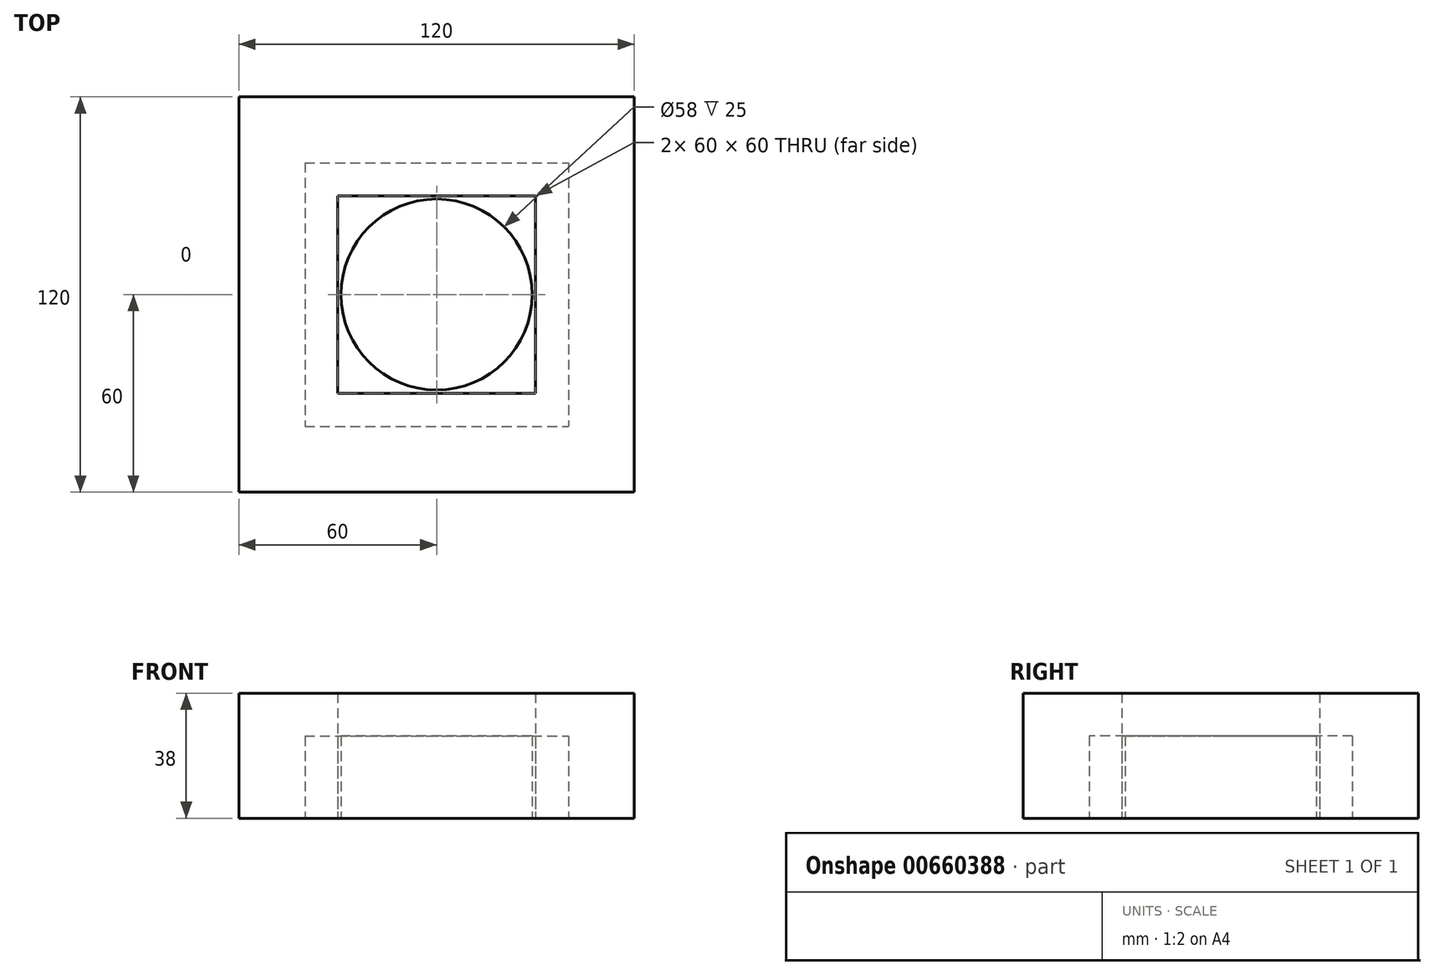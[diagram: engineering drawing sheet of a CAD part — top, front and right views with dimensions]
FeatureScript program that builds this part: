
annotation { "Feature Type Name" : "Feature", "Feature Type Description" : "" }
export const myFeature = defineFeature(function(context is Context, id is Id, definition is map)
    precondition{}
    {
        {
            var Q0;
            Q0=qCreatedBy(makeId("Top.planeOp"),FACE);
            var sketch = newSketch(context, id + "F0", { "sketchPlane" : qUnion([Q0])});
            skLineSegment(sketch, "E0.bottom", {"start": v(-60, 60) * mm, "end": v(60, 60) * mm});
            skLineSegment(sketch, "E0.top", {"start": v(-60, -60) * mm, "end": v(60, -60) * mm});
            skLineSegment(sketch, "E0.left", {"start": v(-60, 60) * mm, "end": v(-60, -60) * mm});
            skLineSegment(sketch, "E0.right", {"start": v(60, 60) * mm, "end": v(60, -60) * mm});
            skLineSegment(sketch, "E1.bottom", {"start": v(-40, 40) * mm, "end": v(40, 40) * mm});
            skLineSegment(sketch, "E1.top", {"start": v(-40, -40) * mm, "end": v(40, -40) * mm});
            skLineSegment(sketch, "E1.left", {"start": v(-40, 40) * mm, "end": v(-40, -40) * mm});
            skLineSegment(sketch, "E1.right", {"start": v(40, 40) * mm, "end": v(40, -40) * mm});
            skLineSegment(sketch, "E2.bottom", {"start": v(-30, -30) * mm, "end": v(30, -30) * mm});
            skLineSegment(sketch, "E2.top", {"start": v(-30, 30) * mm, "end": v(30, 30) * mm});
            skLineSegment(sketch, "E2.left", {"start": v(-30, -30) * mm, "end": v(-30, 30) * mm});
            skLineSegment(sketch, "E2.right", {"start": v(30, -30) * mm, "end": v(30, 30) * mm});
            skCircle(sketch, "E3", {"center": v(0, 0) * mm, "radius": 29 * mm});
            skSolve(sketch);
        }
        {
            var Q0;
            Q0=makeQuery(id+"F0.imprint","IMPRINT",FACE,{"disambiguationData":[TD([[makeQuery(id+"F0.imprint","IMPRINT",EDGE,{"derivedFrom":sQuery(id+"F0.wireOp",EDGE,"E0.bottom")}),-1.0]])]});
            var Q1;
            Q1=makeQuery(id+"F0.imprint","IMPRINT",FACE,{"disambiguationData":[TD([[makeQuery(id+"F0.imprint","IMPRINT",EDGE,{"derivedFrom":sQuery(id+"F0.wireOp",EDGE,"E1.bottom")}),-1.0]])]});
            extrude(context, id + "F1", {"entities" : qUnion([Q0, Q1]), "depth" : 38 * mm, "offsetDistance" : 25 * mm});
        }
        {
            var Q0;
            Q0=makeQuery(id+"F0.imprint","IMPRINT",FACE,{"disambiguationData":[TD([[makeQuery(id+"F0.imprint","IMPRINT",EDGE,{"derivedFrom":sQuery(id+"F0.wireOp",EDGE,"E1.bottom")}),-1.0]])]});
            extrude(context, id + "F2", {"entities" : qUnion([Q0]), "depth" : 25 * mm, "offsetDistance" : 25 * mm});
        }
        {
            var Q0;
            Q0=makeQuery(id+"F0.imprint","IMPRINT",FACE,{"disambiguationData":[TD([[makeQuery(id+"F0.imprint","IMPRINT",EDGE,{"derivedFrom":sQuery(id+"F0.wireOp",EDGE,"E2.bottom")}),1.0]])]});
            extrude(context, id + "F3", {"entities" : qUnion([Q0]), "depth" : 25 * mm, "offsetDistance" : 25 * mm});
        }
    });
